SOLIDWORKS PART (.sldprt)
format: sldprt  version: not decoded by parser v0  size: 745,472 bytes
history: native  units: mm
features: sketch x8, extrude x5, revolve x2, plane x2, mirror x2, material x1, cut_extrude x1, fillet x1, pattern_linear x1 (+16 scaffold rows collapsed)
feature tree (39):
  scaffold x16  (default folders/planes/origin — collapsed)
  material  "Material <not specified>"
  sketch  "Sketch1"  dims[D1=1764.0mm D2=4000.0mm D3=3000.0mm D4=14.0mm]
  revolve  "Revolve1"  Angle=360deg
  plane  "Plane1"  Offset=1400mm
  plane  "Plane2"  Offset=1400mm
  sketch  "Sketch2"  dims[D1=14.0mm]
  extrude  "Extrude1"  Depth=250mm
  sketch  "Sketch3"  dims[D1=2085.0mm D2=800.0mm D3=1400.0mm]
  extrude  "Extrude2"  Depth=10mm
  sketch  "Sketch5"  dims[D1=15.0mm]
  extrude  "Extrude3"  Depth=175mm
  sketch  "Sketch6"  dims[D1=30.0mm D2=250.0mm D3=1200.0mm]
  cut_extrude  "Cut-Extrude5"  [1 undecoded]
  sketch  "Sketch7"  dims[D1=15.0mm D2=15.0mm D3=80.0mm D4=200.0mm D5=15.0mm D6=15.0mm D7=550.0mm D8=900.0mm]
  extrude  "Extrude4"  [1 undecoded]
  mirror  "Mirror1"
  sketch  "Sketch8"  dims[D1=1050.0mm D2=326.8mm D3=581.3mm D4=1.0mm D5=75.5mm D6=33.0mm D7=2.0mm D8=35.5mm D9=1090.0mm D10=400.0mm D11=12.0mm]
  revolve  "Revolve2"  Angle=360deg
  sketch  "Sketch9"  dims[D1=25.0mm D2=10.0mm]
  extrude  "Extrude5"  Depth=5mm
  fillet  "Fillet1"  Radius=4mm
  pattern_linear  "LPattern1"  Count1=2 Count2=1 Spacing1=2200mm Spacing2=10mm
  mirror  "Mirror2"
decode coverage: 16 of 20 modeling features carry decoded parameters
note: 2 parameter values undecoded
note: suppression state not decoded; provenance and decode notes live in map.json
